# Revit family: Towel_Ring-Wall_Mounted-American_Standard-CS_Series-8335.190
name_source: partatom
category: Specialty Equipment
revit_build: Autodesk Revit 2018 (Build: 20170223_1515(x64)
units: mm (PartAtom-declared; Revit-internal decimal feet)

## family parameters
Cut with Voids When Loaded = No
Host = Face
OmniClass Number = 23.40.20.21.27
OmniClass Title = Towel Bars
Part Type = Normal
Room Calculation Point = No
Round Connector Dimension = Use Diameter
Shared = Yes

## types (2) — shared parameters
Assembly Code = C1030220
Default Elevation = 40"
Description = CS Series Towel Ring.
Height = 8 1/8"
Installation Type = Wall Mounted
Length = 3 3/16"
Manufacturer = American Standard
Price = Prices may vary. Please consult Manufacturer Representative for most up-to-date price list.
Product Documentation Link = https://www.americanstandard-us.com
Product Page URL = https://www.americanstandard-us.com
Revised Date = 05/03/2021
URL = http://www.americanstandard-us.com
Warranty Information = 1 Year Limited Warranty
Width = 7 1/8"

## per-type parameters (varying)
| type | Body Material |
| 8335.190.002 | Metal-American_Standard-002-Polished_Chrome |
| 8335.190.295 | Metal-American_Standard-295-Brushed_Nickel |

note: column(s) folded — value = type name in every type: Model

## geometry (parser evidence)
native form markers: Sweep x3
no freeform markers — native parametric forms only
